# Revit family: for update_39863USA_new
name_source: partatom
category: Plumbing Fixtures
revit_build: Autodesk Revit 2018 (Build: 20170223_1515(x64)
units: mm (PartAtom-declared; Revit-internal decimal feet)

## family parameters
Always vertical = No
Cut with Voids When Loaded = No
OmniClass Number = 23.31.11.00
OmniClass Title = Faucets
Part Type = Normal
Room Calculation Point = No
Round Connector Dimension = Use Diameter
Shared = No
Work Plane-Based = Yes

## types (5) — shared parameters
Always visible = Yes
BIMobject category = Taps & Mixers
Connector Description = Water Inlet 9.5mm
Default Elevation = 1219.2 mm  [stored 4 ft]
Description = AXOR Citterio Single lever kitchen mixer Select 230 2jet with pull-out spray
Design country = Germany
Diameter = 10 mm
EAN code = 4059625427156
Edition number = 1
IFC Classification = Valve
Manufacturer = AXOR
Manufacturer country = Germany
Manufacturer name = AXOR
Material main = Brass
Material secondary = Chrome
Model = 39863USA
OmniClass Code = 23-31 11 00
OmniClass Description = Faucets
Product Guid = d6aeaa10-c04a-42e2-aa64-7e594a7a5fe4
Product SKU = 39863USA
Product data url = https://bimobject.com
Product family = AXOR Citterio
Product group = Kitchen mixers
Product name = 39863USA AXOR Citterio Single lever kitchen mixer Select 230 2jet with pull-out spray
QR code = https://bimobject.com
URL = https://www.axor-design.com
Weight Net (Kg) = 2.9

## per-type parameters (varying)
| type | Material 1 |
| 001 Chrome | AXOR - Metal - 001 Chrome |
| 251 Matt Black/Brushed Gold Optic | AXOR - Metal - 251 Matt Black/Brushed Gold Optic |
| 671 Matt Black | AXOR - Metal - 671 Matt Black |
| 801 Stainless Steel Finish | AXOR - Metal - 801 Stainless Steel Optic |
| 831 Polished Nickel | AXOR - Metal - 831 Polished Nickel |

note: [stored X ft] marks values corroborated as IEEE doubles in the binary element streams (Revit-internal decimal feet)

## geometry (parser evidence)
native form markers: Sweep x1
no freeform markers — native parametric forms only
